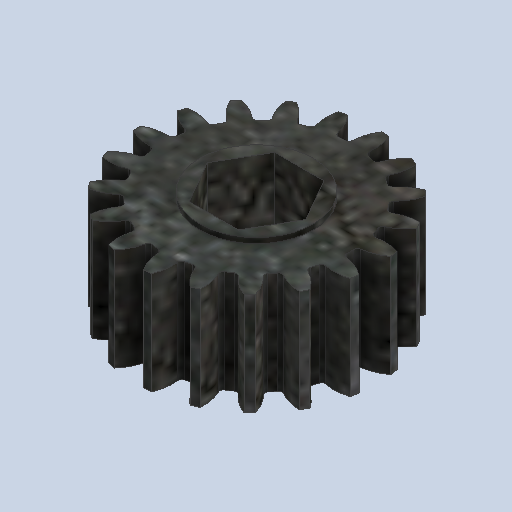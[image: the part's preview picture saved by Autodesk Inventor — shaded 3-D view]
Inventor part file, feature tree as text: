
AUTODESK INVENTOR PART (.ipt)
format: ipt  version: 2024 (Build 280153000, 153)  size: 349,696 bytes
history: native  units: in
note: dims shown in document units (in); Inventor stores cm internally (conversion verified against a paired STEP export)
features: fillet x1
ambient origin geometry x8: Origin, YZ Plane, XZ Plane, XY Plane, X Axis, Y Axis, Z Axis, Center Point
bodies: Solid1 (feature_tree)
feature tree (1):
  fillet  "Fillet1"  [1 undecoded]
note: 1 required parameter value undecoded (feature->parameter linkage not recoverable at this tier; creation-order binding heuristic only, values carry confidence <= 0.55)
